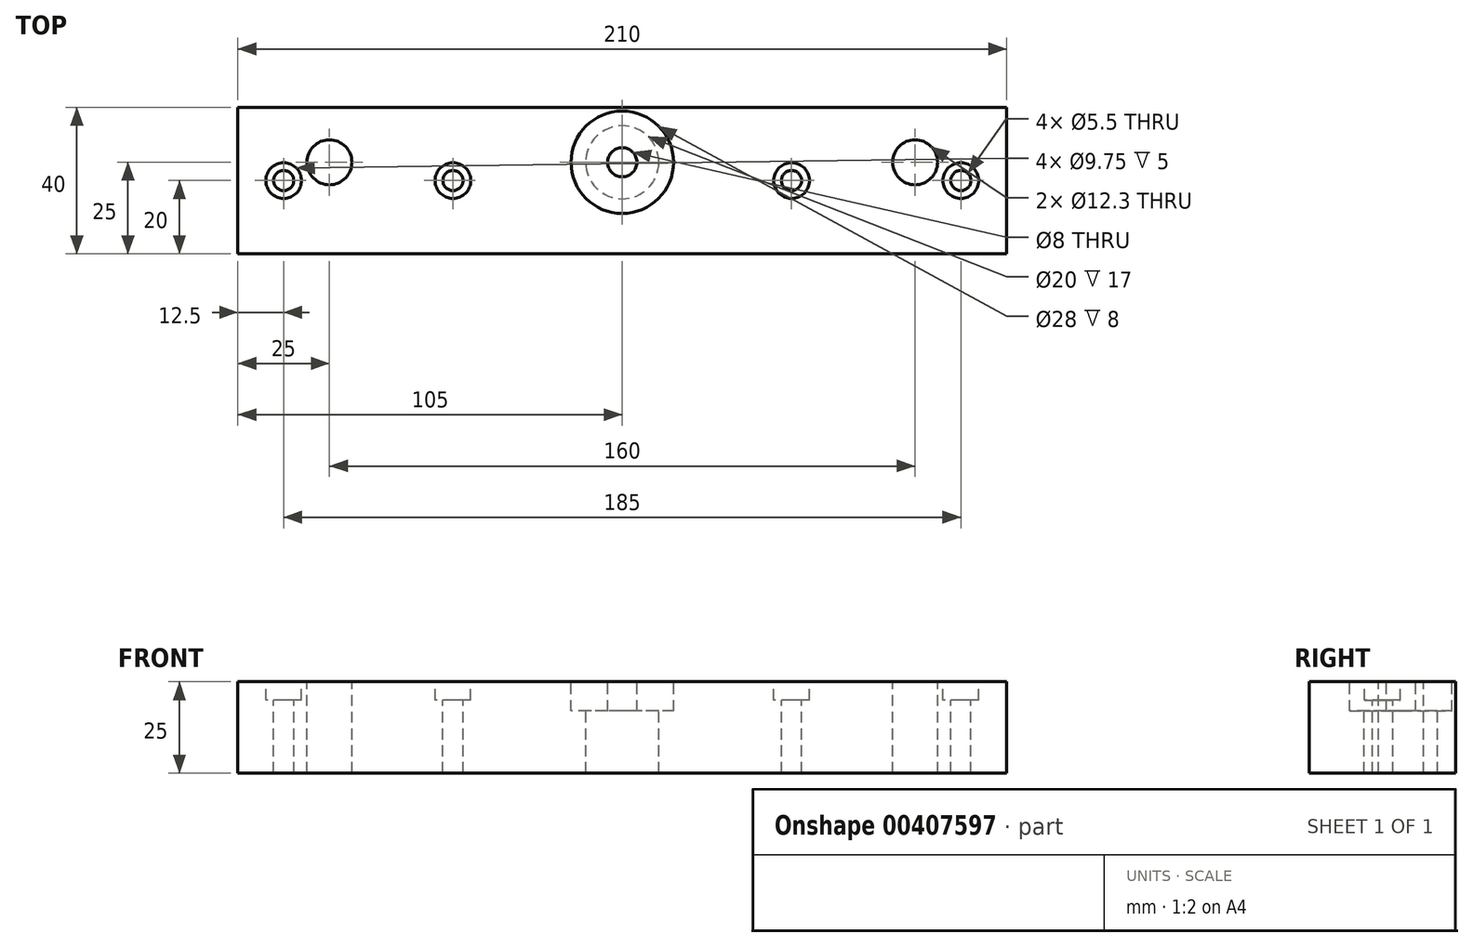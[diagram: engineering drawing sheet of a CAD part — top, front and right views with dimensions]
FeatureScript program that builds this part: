
annotation { "Feature Type Name" : "Feature", "Feature Type Description" : "" }
export const myFeature = defineFeature(function(context is Context, id is Id, definition is map)
    precondition{}
    {
        {
            var Q0;
            Q0=qCreatedBy(makeId("Top.planeOp"),FACE);
            var sketch = newSketch(context, id + "F0", { "sketchPlane" : qUnion([Q0])});
            skLineSegment(sketch, "E0.bottom", {"start": v(105, -20) * mm, "end": v(-105, -20) * mm});
            skLineSegment(sketch, "E0.top", {"start": v(105, 20) * mm, "end": v(-105, 20) * mm});
            skLineSegment(sketch, "E0.left", {"start": v(105, -20) * mm, "end": v(105, 20) * mm});
            skLineSegment(sketch, "E0.right", {"start": v(-105, -20) * mm, "end": v(-105, 20) * mm});
            skPoint(sketch, "E0.middle", {"position": v(0, 0) * mm});
            skCircle(sketch, "E1", {"center": v(-80, 5) * mm, "radius": 6.15 * mm});
            skCircle(sketch, "E2", {"center": v(0, 5) * mm, "radius": 14 * mm});
            skCircle(sketch, "E3", {"center": v(80, 5) * mm, "radius": 6.15 * mm});
            skCircle(sketch, "E4", {"center": v(0, 5) * mm, "radius": 4 * mm});
            skLineSegment(sketch, "E5", {"start": v(-105, 5) * mm, "end": v(105, 5) * mm, "construction": true});
            skLineSegment(sketch, "E6", {"start": v(-105, 0) * mm, "end": v(105, 0) * mm, "construction": true});
            skPoint(sketch, "E7", {"position": v(-92.5, 0) * mm});
            skPoint(sketch, "E8", {"position": v(-46.25, 0) * mm});
            skPoint(sketch, "E9", {"position": v(46.25, 0) * mm});
            skPoint(sketch, "E10", {"position": v(92.5, 0) * mm});
            skCircle(sketch, "E11", {"center": v(0, 5) * mm, "radius": 10 * mm});
            skSolve(sketch);
        }
        {
            var Q0;
            Q0=makeQuery(id+"F0.imprint","IMPRINT",FACE,{"disambiguationData":[TD([[makeQuery(id+"F0.imprint","IMPRINT",EDGE,{"derivedFrom":sQuery(id+"F0.wireOp",EDGE,"E0.bottom")}),-1.0]])]});
            var Q1;
            Q1=makeQuery(id+"F0.imprint","IMPRINT",FACE,{"disambiguationData":[TD([[makeQuery(id+"F0.imprint","IMPRINT",EDGE,{"derivedFrom":sQuery(id+"F0.wireOp",EDGE,"E2")}),-1.0]])]});
            var Q2;
            Q2=makeQuery(id+"F0.imprint","IMPRINT",FACE,{"disambiguationData":[TD([[makeQuery(id+"F0.imprint","IMPRINT",EDGE,{"derivedFrom":sQuery(id+"F0.wireOp",EDGE,"E2")}),1.0]])]});
            extrude(context, id + "F1", {"entities" : qUnion([Q0, Q1, Q2]), "oppositeDirection" : true, "depth" : 25 * mm});
        }
        {
            var Q0;
            Q0=makeQuery(id+"F0.imprint","IMPRINT",FACE,{"disambiguationData":[TD([[makeQuery(id+"F0.imprint","IMPRINT",EDGE,{"derivedFrom":sQuery(id+"F0.wireOp",EDGE,"E2")}),1.0]])]});
            extrude(context, id + "F2", {"entities" : qUnion([Q0]), "operationType" : NewBodyOperationType.REMOVE, "oppositeDirection" : true, "depth" : 8 * mm});
        }
        {
            var Q0;
            Q0=sQuery(id+"F0.wireOp",VERTEX,"E7");
            var Q1;
            Q1=sQuery(id+"F0.wireOp",VERTEX,"E8");
            var Q2;
            Q2=sQuery(id+"F0.wireOp",VERTEX,"E9");
            var Q3;
            Q3=sQuery(id+"F0.wireOp",VERTEX,"E10");
            var Q4;
            Q4=makeQuery(id+"F1.opExtrude","SWEPT_BODY",BODY,{"disambiguationData":[OSD([sQuery(id+"F0.wireOp",EDGE,"E0.bottom"),sQuery(id+"F0.wireOp",EDGE,"E0.top"),sQuery(id+"F0.wireOp",EDGE,"E0.left"),sQuery(id+"F0.wireOp",EDGE,"E0.right"),sQuery(id+"F0.wireOp",EDGE,"E1"),sQuery(id+"F0.wireOp",EDGE,"E2"),sQuery(id+"F0.wireOp",EDGE,"E3")])]});
            hole(context, id + "F3", {"style" : HoleStyle.C_BORE, "endStyle" : HoleEndStyle.THROUGH, "standardTappedOrClearance" : lookupTablePath({ "standard" : "ISO", "fit" : "Normal", "size" : "M5", "type" : "Clearance" }), "standardBlindInLast" : lookupTablePath({ "fit" : "Standard", "standard" : "ISO", "size" : "M5", "type" : "Clearance" }), "holeDiameter" : 5.5 * mm, "cBoreDiameter" : 9.75 * mm, "cBoreDepth" : 5 * mm, "isTappedThrough" : true, "tappedDepth" : 12 * mm, "tapClearance" : 3, "locations" : qUnion([Q0, Q1, Q2, Q3]), "scope" : qUnion([Q4])});
        }
        {
            var Q0;
            Q0=makeQuery(id+"F0.imprint","IMPRINT",FACE,{"disambiguationData":[TD([[makeQuery(id+"F0.imprint","IMPRINT",EDGE,{"derivedFrom":sQuery(id+"F0.wireOp",EDGE,"E2")}),1.0]])]});
            var Q1;
            Q1=makeQuery(id+"F0.imprint","IMPRINT",FACE,{"disambiguationData":[TD([[makeQuery(id+"F0.imprint","IMPRINT",EDGE,{"derivedFrom":sQuery(id+"F0.wireOp",EDGE,"E4")}),-1.0]])]});
            extrude(context, id + "F4", {"entities" : qUnion([Q0, Q1]), "oppositeDirection" : true, "depth" : 8 * mm});
        }
    });
